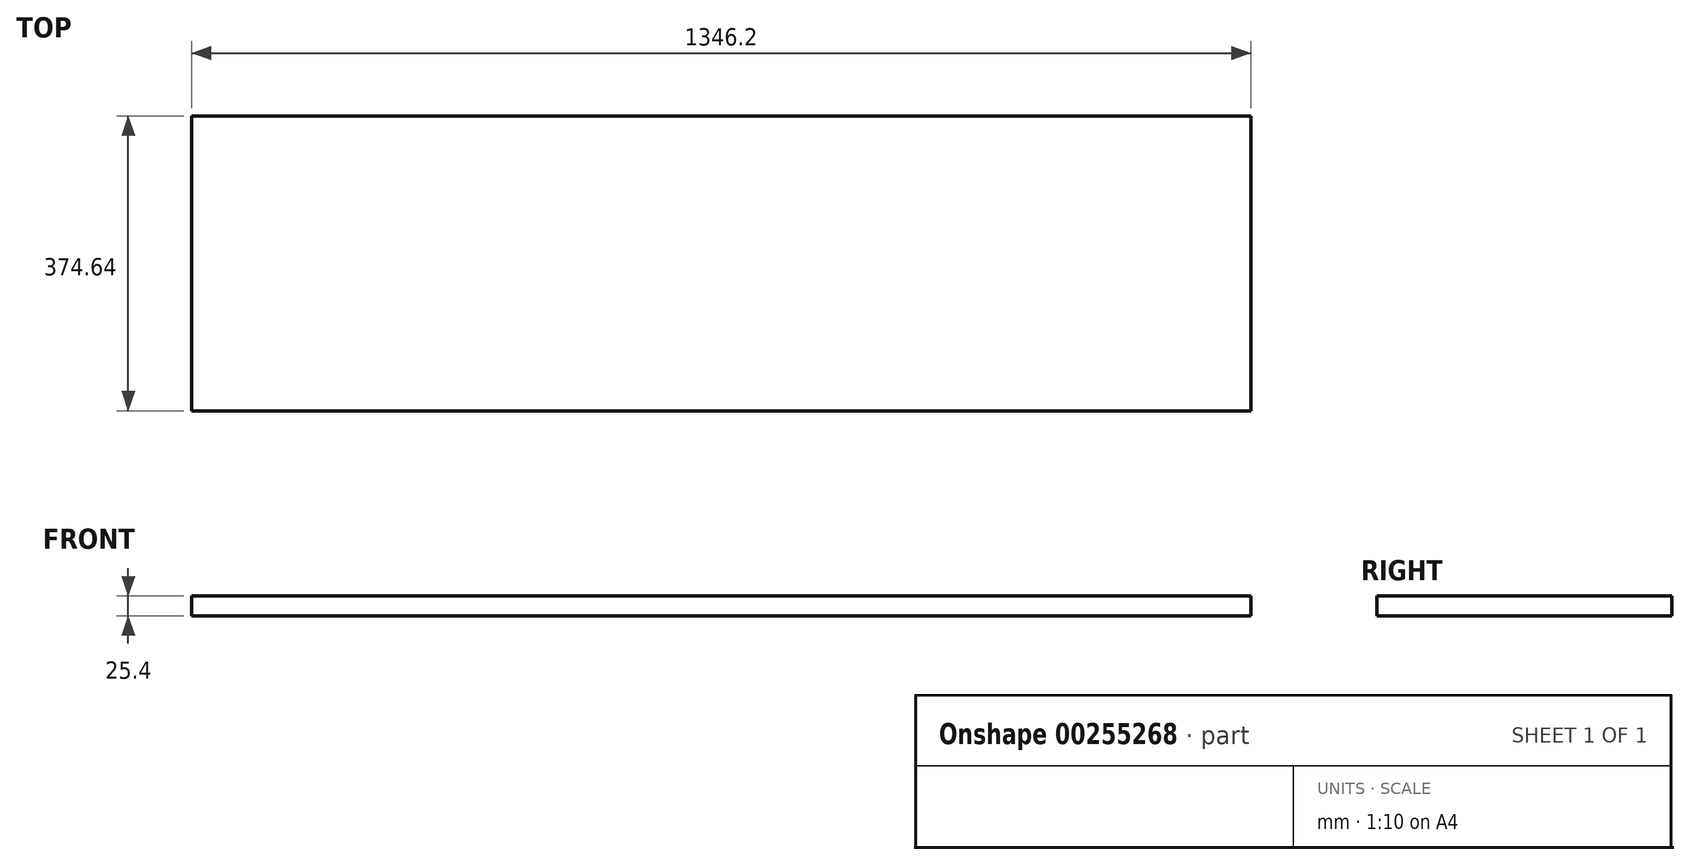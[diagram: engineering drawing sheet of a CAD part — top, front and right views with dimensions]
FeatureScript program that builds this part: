
annotation { "Feature Type Name" : "Feature", "Feature Type Description" : "" }
export const myFeature = defineFeature(function(context is Context, id is Id, definition is map)
    precondition{}
    {
        {
            var Q0;
            Q0=qCreatedBy(makeId("Top.planeOp"),FACE);
            var sketch = newSketch(context, id + "F1", { "sketchPlane" : qUnion([Q0])});
            skLineSegment(sketch, "E0.bottom", {"start": v(673.1, 187.32) * mm, "end": v(-673.1, 187.32) * mm});
            skLineSegment(sketch, "E0.top", {"start": v(673.1, -187.33) * mm, "end": v(-673.1, -187.33) * mm});
            skLineSegment(sketch, "E0.left", {"start": v(673.1, 187.32) * mm, "end": v(673.1, -187.33) * mm});
            skLineSegment(sketch, "E0.right", {"start": v(-673.1, 187.32) * mm, "end": v(-673.1, -187.33) * mm});
            skPoint(sketch, "E0.middle", {"position": v(0, 0) * mm});
            skSolve(sketch);
        }
        {
            var Q0;
            Q0=qSketchRegion(id+"F1",true);
            extrude(context, id + "F0", {"entities" : qUnion([Q0]), "depth" : 25.4 * mm});
        }
    });
